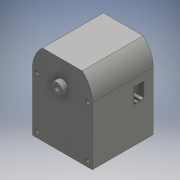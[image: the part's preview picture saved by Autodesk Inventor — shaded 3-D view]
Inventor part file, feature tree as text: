
AUTODESK INVENTOR PART (.ipt)
format: ipt  version: 2016 (Build 200138000, 138)  size: 233,472 bytes
history: native  units: mm
features: extrude x10, sketch x10, other x1
ambient origin geometry x8: Origin, YZ Plane, XZ Plane, XY Plane, X Axis, Y Axis, Z Axis, Center Point
bodies: Body1 (feature_tree)
feature tree (21):
  other  "ソリッド1"
  extrude  "押し出し1"  Depth=32.0mm
  extrude  "押し出し2"  Depth=43.0mm
  extrude  "押し出し3"  Depth=32.5mm TaperAngle=0.0deg
  extrude  "押し出し4"  Depth=9.5mm
  extrude  "押し出し5"  Depth=32.5mm TaperAngle=0.0deg
  extrude  "押し出し6"  Depth=8.5mm
  extrude  "押し出し7"  Depth=13.5mm
  extrude  "押し出し8"  Depth=2.0mm
  extrude  "押し出し9"  Depth=13.5mm
  extrude  "押し出し11"  Depth=2.0mm
  sketch  "スケッチ1"
  sketch  "スケッチ2"
  sketch  "スケッチ3"
  sketch  "スケッチ4"
  sketch  "スケッチ5"
  sketch  "スケッチ6"
  sketch  "スケッチ7"
  sketch  "スケッチ8"
  sketch  "スケッチ9"
  sketch  "スケッチ10"
